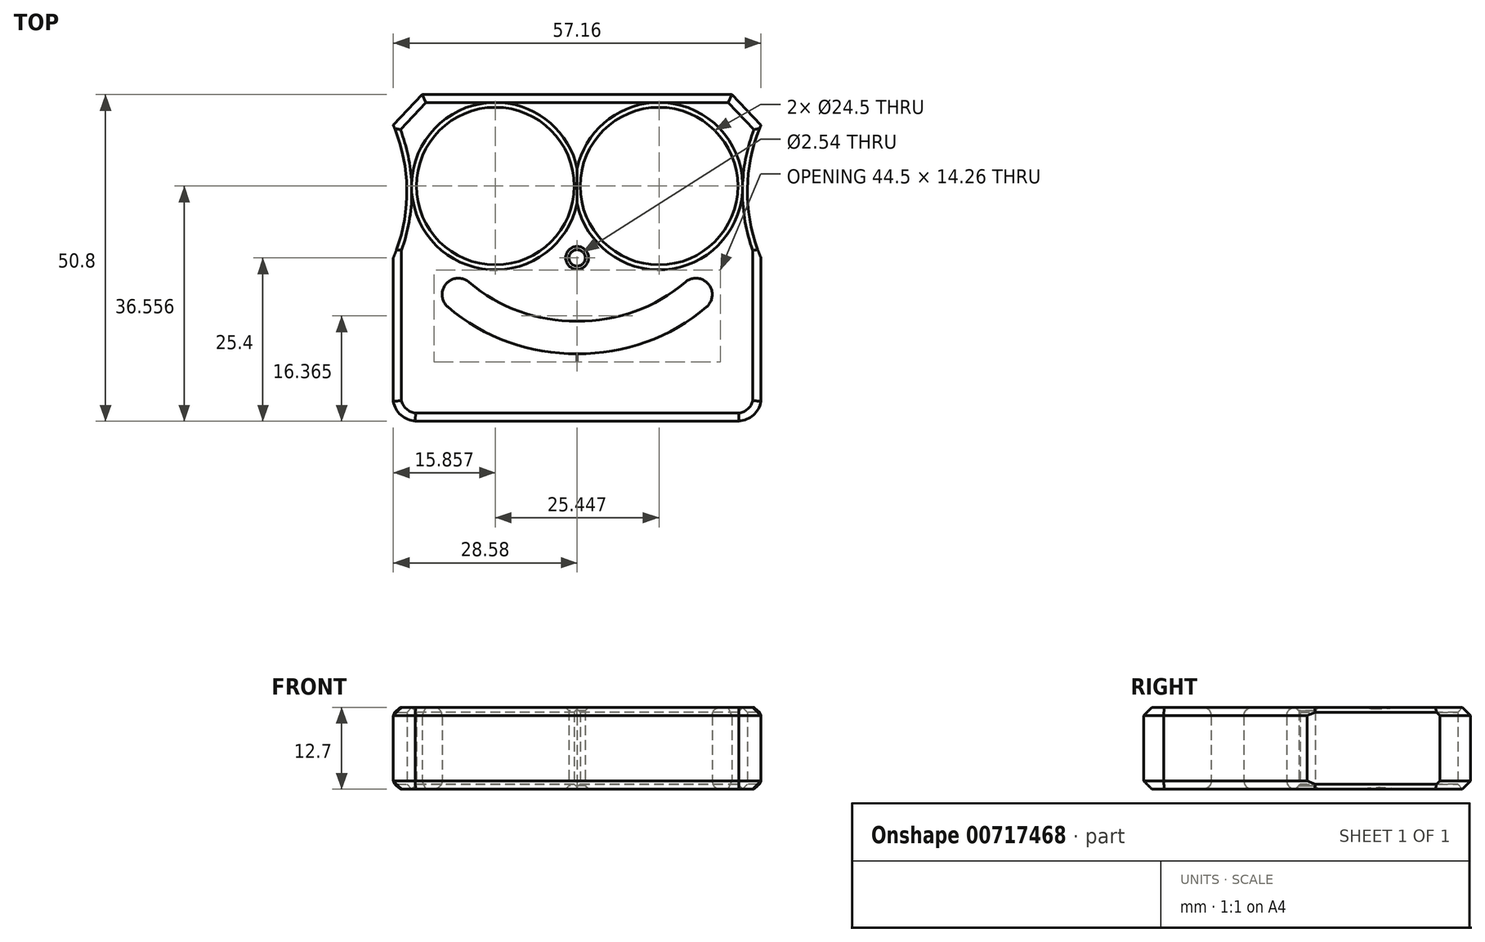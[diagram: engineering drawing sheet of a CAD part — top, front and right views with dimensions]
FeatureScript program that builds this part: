
annotation { "Feature Type Name" : "Feature", "Feature Type Description" : "" }
export const myFeature = defineFeature(function(context is Context, id is Id, definition is map)
    precondition{}
    {
        {
            var Q0;
            Q0=qCreatedBy(makeId("Top.planeOp"),FACE);
            var sketch = newSketch(context, id + "F0", { "sketchPlane" : qUnion([Q0])});
            skPoint(sketch, "E0.middle", {"position": v(0, 0) * mm});
            skCircle(sketch, "E1", {"center": v(-12.72, 11.16) * mm, "radius": 12.25 * mm});
            skCircle(sketch, "E2.MirrorC", {"center": v(12.72, 11.16) * mm, "radius": 12.25 * mm});
            skLineSegment(sketch, "E3", {"start": v(-28.58, 20.63) * mm, "end": v(-24.05, 25.4) * mm});
            skLineSegment(sketch, "E4.MirrorCS", {"start": v(28.58, 20.63) * mm, "end": v(24.05, 25.4) * mm});
            skArc(sketch, "E5", {"start": v(-28.58, 0) * mm, "mid": v(-26.46, 10.32) * mm, "end": v(-28.58, 20.63) * mm});
            skArc(sketch, "E6.MirrorCS", {"start": v(28.58, 0) * mm, "mid": v(26.46, 10.32) * mm, "end": v(28.58, 20.63) * mm});
            skArc(sketch, "E7", {"start": v(-28.58, -22.31) * mm, "mid": v(-27.39, -24.43) * mm, "end": v(-25.16, -25.4) * mm});
            skArc(sketch, "E8.MirrorCS", {"start": v(28.58, -22.31) * mm, "mid": v(27.39, -24.43) * mm, "end": v(25.16, -25.4) * mm});
            skLineSegment(sketch, "E9", {"start": v(-28.58, 0) * mm, "end": v(-28.58, -22.31) * mm});
            skLineSegment(sketch, "E10", {"start": v(-24.05, 25.4) * mm, "end": v(24.05, 25.4) * mm});
            skLineSegment(sketch, "E11", {"start": v(28.58, 0) * mm, "end": v(28.58, -22.31) * mm});
            skLineSegment(sketch, "E12", {"start": v(-25.16, -25.4) * mm, "end": v(25.16, -25.4) * mm});
            skArc(sketch, "E13", {"start": v(-18.45, -5.7) * mm, "mid": v(-9.83, -10.72) * mm, "end": v(0, -12.35) * mm});
            skArc(sketch, "E14.MirrorCS", {"start": v(18.45, -5.7) * mm, "mid": v(9.83, -10.72) * mm, "end": v(0, -12.35) * mm});
            skArc(sketch, "E15.0.startCap", {"start": v(-20.1, -7.63) * mm, "mid": v(-20.38, -4.05) * mm, "end": v(-16.8, -3.78) * mm});
            skArc(sketch, "E15.0.endCap", {"start": v(-0.04, -9.81) * mm, "mid": v(2.54, -12.31) * mm, "end": v(0.04, -14.9) * mm});
            skArc(sketch, "E15.0.left", {"start": v(-16.8, -3.78) * mm, "mid": v(-8.97, -8.33) * mm, "end": v(-0.04, -9.81) * mm});
            skArc(sketch, "E15.0.right", {"start": v(-20.1, -7.63) * mm, "mid": v(-10.7, -13.1) * mm, "end": v(0.04, -14.9) * mm});
            skArc(sketch, "E15.1.startCap", {"start": v(16.8, -3.78) * mm, "mid": v(20.38, -4.05) * mm, "end": v(20.1, -7.63) * mm});
            skArc(sketch, "E15.1.endCap", {"start": v(-0.04, -14.9) * mm, "mid": v(-2.54, -12.31) * mm, "end": v(0.04, -9.81) * mm});
            skArc(sketch, "E15.1.left", {"start": v(20.1, -7.63) * mm, "mid": v(10.7, -13.1) * mm, "end": v(-0.04, -14.9) * mm});
            skArc(sketch, "E15.1.right", {"start": v(16.8, -3.78) * mm, "mid": v(8.97, -8.33) * mm, "end": v(0.04, -9.81) * mm});
            skCircle(sketch, "E16", {"center": v(0, 0) * mm, "radius": 1.27 * mm});
            skSolve(sketch);
        }
        {
            var Q0;
            Q0=makeQuery(id+"F0.imprint","IMPRINT",FACE,{"disambiguationData":[TD([[makeQuery(id+"F0.imprint","IMPRINT",EDGE,{"derivedFrom":sQuery(id+"F0.wireOp",EDGE,"E1")}),-1.0]])]});
            extrude(context, id + "F1", {"entities" : qUnion([Q0]), "depth" : 12.7 * mm, "offsetDistance" : 25.4 * mm});
        }
        {
            var Q0;
            Q0=makeQuery(id+"F1.opExtrude","CAP_EDGE",EDGE,{"disambiguationData":[OSD([sQuery(id+"F0.wireOp",EDGE,"E7")])],"isStart":false});
            var Q1;
            Q1=makeQuery(id+"F1.opExtrude","CAP_EDGE",EDGE,{"disambiguationData":[OSD([sQuery(id+"F0.wireOp",EDGE,"E9")])],"isStart":false});
            var Q2;
            Q2=makeQuery(id+"F1.opExtrude","CAP_EDGE",EDGE,{"disambiguationData":[OSD([sQuery(id+"F0.wireOp",EDGE,"E7")])],"isStart":true});
            var Q3;
            Q3=makeQuery(id+"F1.opExtrude","CAP_EDGE",EDGE,{"disambiguationData":[OSD([sQuery(id+"F0.wireOp",EDGE,"E9")])],"isStart":true});
            var Q4;
            Q4=makeQuery(id+"F1.opExtrude","CAP_EDGE",EDGE,{"disambiguationData":[OSD([sQuery(id+"F0.wireOp",EDGE,"E12")])],"isStart":false});
            var Q5;
            Q5=makeQuery(id+"F1.opExtrude","CAP_EDGE",EDGE,{"disambiguationData":[OSD([sQuery(id+"F0.wireOp",EDGE,"E12")])],"isStart":true});
            var Q6;
            Q6=makeQuery(id+"F1.opExtrude","CAP_EDGE",EDGE,{"disambiguationData":[OSD([sQuery(id+"F0.wireOp",EDGE,"E8.MirrorCS")])],"isStart":true});
            var Q7;
            Q7=makeQuery(id+"F1.opExtrude","CAP_EDGE",EDGE,{"disambiguationData":[OSD([sQuery(id+"F0.wireOp",EDGE,"E8.MirrorCS")])],"isStart":false});
            var Q8;
            Q8=makeQuery(id+"F1.opExtrude","CAP_EDGE",EDGE,{"disambiguationData":[OSD([sQuery(id+"F0.wireOp",EDGE,"E11")])],"isStart":false});
            var Q9;
            Q9=makeQuery(id+"F1.opExtrude","CAP_EDGE",EDGE,{"disambiguationData":[OSD([sQuery(id+"F0.wireOp",EDGE,"E11")])],"isStart":true});
            var Q10;
            Q10=makeQuery(id+"F1.opExtrude","CAP_EDGE",EDGE,{"disambiguationData":[OSD([sQuery(id+"F0.wireOp",EDGE,"E3")])],"isStart":false});
            var Q11;
            Q11=makeQuery(id+"F1.opExtrude","CAP_EDGE",EDGE,{"disambiguationData":[OSD([sQuery(id+"F0.wireOp",EDGE,"E3")])],"isStart":true});
            var Q12;
            Q12=makeQuery(id+"F1.opExtrude","CAP_EDGE",EDGE,{"disambiguationData":[OSD([sQuery(id+"F0.wireOp",EDGE,"E10")])],"isStart":true});
            var Q13;
            Q13=makeQuery(id+"F1.opExtrude","CAP_EDGE",EDGE,{"disambiguationData":[OSD([sQuery(id+"F0.wireOp",EDGE,"E10")])],"isStart":false});
            var Q14;
            Q14=makeQuery(id+"F1.opExtrude","CAP_EDGE",EDGE,{"disambiguationData":[OSD([sQuery(id+"F0.wireOp",EDGE,"E4.MirrorCS")])],"isStart":false});
            var Q15;
            Q15=makeQuery(id+"F1.opExtrude","CAP_EDGE",EDGE,{"disambiguationData":[OSD([sQuery(id+"F0.wireOp",EDGE,"E4.MirrorCS")])],"isStart":true});
            chamfer(context, id + "F2", {"entities" : qUnion([Q0, Q1, Q2, Q3, Q4, Q5, Q6, Q7, Q8, Q9, Q10, Q11, Q12, Q13, Q14, Q15]), "width" : 1.27 * mm, "tangentPropagation" : true});
        }
        {
            var Q0;
            Q0=makeQuery(id+"F1.opExtrude","CAP_EDGE",EDGE,{"disambiguationData":[OSD([sQuery(id+"F0.wireOp",EDGE,"E5")])],"isStart":true});
            var Q1;
            Q1=makeQuery(id+"F1.opExtrude","CAP_EDGE",EDGE,{"disambiguationData":[OSD([sQuery(id+"F0.wireOp",EDGE,"E5")])],"isStart":false});
            var Q2;
            Q2=makeQuery(id+"F1.opExtrude","CAP_EDGE",EDGE,{"disambiguationData":[OSD([sQuery(id+"F0.wireOp",EDGE,"E1")])],"isStart":false});
            var Q3;
            Q3=makeQuery(id+"F1.opExtrude","CAP_EDGE",EDGE,{"disambiguationData":[OSD([sQuery(id+"F0.wireOp",EDGE,"E1")])],"isStart":true});
            var Q4;
            Q4=makeQuery(id+"F1.opExtrude","CAP_EDGE",EDGE,{"disambiguationData":[OSD([sQuery(id+"F0.wireOp",EDGE,"E2.MirrorC")])],"isStart":false});
            var Q5;
            Q5=makeQuery(id+"F1.opExtrude","CAP_EDGE",EDGE,{"disambiguationData":[OSD([sQuery(id+"F0.wireOp",EDGE,"E2.MirrorC")])],"isStart":true});
            var Q6;
            Q6=makeQuery(id+"F1.opExtrude","CAP_EDGE",EDGE,{"disambiguationData":[OSD([sQuery(id+"F0.wireOp",EDGE,"E6.MirrorCS")])],"isStart":false});
            var Q7;
            Q7=makeQuery(id+"F1.opExtrude","CAP_EDGE",EDGE,{"disambiguationData":[OSD([sQuery(id+"F0.wireOp",EDGE,"E6.MirrorCS")])],"isStart":true});
            chamfer(context, id + "F3", {"entities" : qUnion([Q0, Q1, Q2, Q3, Q4, Q5, Q6, Q7]), "width" : 0.76 * mm, "tangentPropagation" : true});
        }
        {
            var Q0;
            Q0=makeQuery(id+"F1.opExtrude","CAP_EDGE",EDGE,{"disambiguationData":[OSD([sQuery(id+"F0.wireOp",EDGE,"E16")])],"isStart":true});
            var Q1;
            Q1=makeQuery(id+"F1.opExtrude","CAP_EDGE",EDGE,{"disambiguationData":[OSD([sQuery(id+"F0.wireOp",EDGE,"E16")])],"isStart":false});
            chamfer(context, id + "F4", {"entities" : qUnion([Q0, Q1]), "width" : 0.5 * mm, "tangentPropagation" : true});
        }
        {
            var Q0;
            Q0=makeQuery(id+"F1.opExtrude","CAP_EDGE",EDGE,{"disambiguationData":[OSD([sQuery(id+"F0.wireOp",EDGE,"E15.0.startCap")])],"isStart":true});
            var Q1;
            Q1=makeQuery(id+"F1.opExtrude","CAP_EDGE",EDGE,{"disambiguationData":[OSD([sQuery(id+"F0.wireOp",EDGE,"E15.0.startCap")])],"isStart":false});
            var Q2;
            Q2=makeQuery(id+"F1.opExtrude","CAP_EDGE",EDGE,{"disambiguationData":[OSD([sQuery(id+"F0.wireOp",EDGE,"E15.0.right")])],"isStart":true});
            var Q3;
            Q3=makeQuery(id+"F1.opExtrude","CAP_EDGE",EDGE,{"disambiguationData":[OSD([sQuery(id+"F0.wireOp",EDGE,"E15.0.right")])],"isStart":false});
            var Q4;
            Q4=makeQuery(id+"F1.opExtrude","CAP_EDGE",EDGE,{"disambiguationData":[OSD([sQuery(id+"F0.wireOp",EDGE,"E15.0.left")])],"isStart":true});
            var Q5;
            Q5=makeQuery(id+"F1.opExtrude","CAP_EDGE",EDGE,{"disambiguationData":[OSD([sQuery(id+"F0.wireOp",EDGE,"E15.0.left")])],"isStart":false});
            var Q6;
            Q6=makeQuery(id+"F1.opExtrude","CAP_EDGE",EDGE,{"disambiguationData":[OSD([sQuery(id+"F0.wireOp",EDGE,"E15.1.right")])],"isStart":false});
            var Q7;
            Q7=makeQuery(id+"F1.opExtrude","CAP_EDGE",EDGE,{"disambiguationData":[OSD([sQuery(id+"F0.wireOp",EDGE,"E15.1.right")])],"isStart":true});
            var Q8;
            Q8=makeQuery(id+"F1.opExtrude","CAP_EDGE",EDGE,{"disambiguationData":[OSD([sQuery(id+"F0.wireOp",EDGE,"E15.1.left")])],"isStart":true});
            var Q9;
            Q9=makeQuery(id+"F1.opExtrude","CAP_EDGE",EDGE,{"disambiguationData":[OSD([sQuery(id+"F0.wireOp",EDGE,"E15.1.left")])],"isStart":false});
            var Q10;
            Q10=makeQuery(id+"F1.opExtrude","CAP_EDGE",EDGE,{"disambiguationData":[OSD([sQuery(id+"F0.wireOp",EDGE,"E15.1.startCap")])],"isStart":true});
            var Q11;
            Q11=makeQuery(id+"F1.opExtrude","CAP_EDGE",EDGE,{"disambiguationData":[OSD([sQuery(id+"F0.wireOp",EDGE,"E15.1.startCap")])],"isStart":false});
            fillet(context, id + "F5", {"entities" : qUnion([Q0, Q1, Q2, Q3, Q4, Q5, Q6, Q7, Q8, Q9, Q10, Q11]), "radius" : 1.27 * mm, "tangentPropagation" : true, "allowEdgeOverflow" : false});
        }
    });
